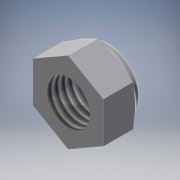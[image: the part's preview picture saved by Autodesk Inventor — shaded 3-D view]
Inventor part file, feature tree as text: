
AUTODESK INVENTOR PART (.ipt)
format: ipt  version: 2016 (Build 200138000, 138)  size: 182,784 bytes
history: native  units: mm
features: extrude x2, sketch x2, fillet x1, thread x1
ambient origin geometry x8: Origin, YZ Plane, XZ Plane, XY Plane, X Axis, Y Axis, Z Axis, Center Point
bodies: Solid1 (feature_tree)
feature tree (6):
  extrude  "Extrusion1"  Depth=13.0mm
  extrude  "Extrusion2"  Depth=2.0mm
  fillet  "Fillet1"  Radius=2.5mm
  thread  "Thread2"  [1 undecoded]
  sketch  "Sketch1"  dims[d0=8.0mm d1=13.0mm]
  sketch  "Sketch2"  dims[d2=5.5mm d3=0.0mm d6=2.0mm d7=2.5mm d8=0.0mm d9=1.5mm d10=10.0mm d11=0.0mm]
note: 1 required parameter value undecoded (feature->parameter linkage not recoverable at this tier; creation-order binding heuristic only, values carry confidence <= 0.55)
